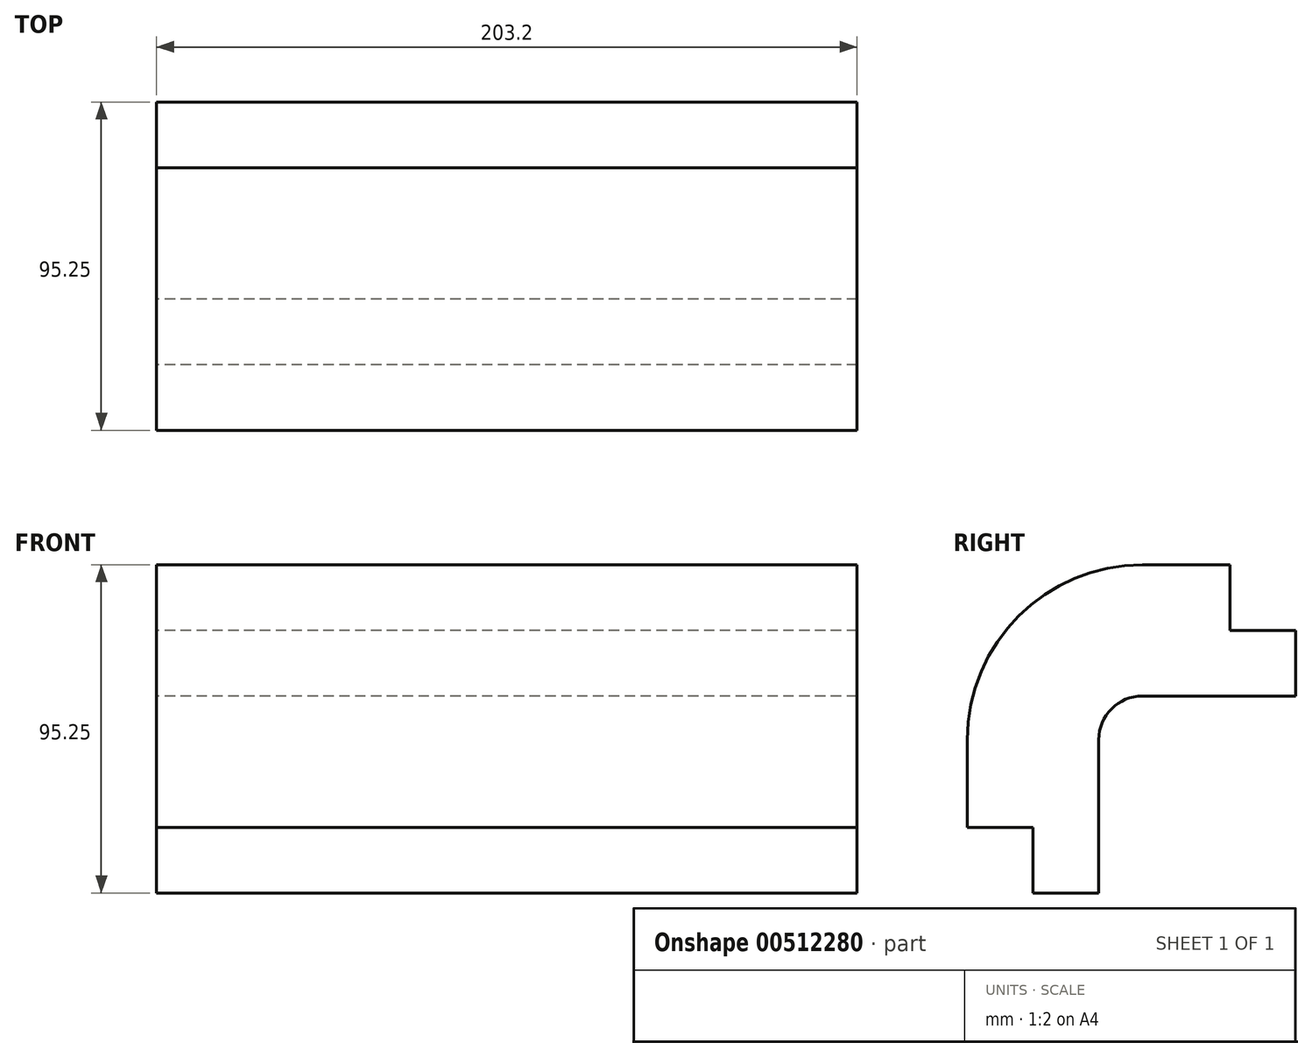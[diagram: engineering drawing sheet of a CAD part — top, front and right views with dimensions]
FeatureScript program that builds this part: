
annotation { "Feature Type Name" : "Feature", "Feature Type Description" : "" }
export const myFeature = defineFeature(function(context is Context, id is Id, definition is map)
    precondition{}
    {
        {
            var Q0;
            Q0=qCreatedBy(makeId("Right.planeOp"),FACE);
            var sketch = newSketch(context, id + "F0", { "sketchPlane" : qUnion([Q0])});
            skLineSegment(sketch, "E0.bottom", {"start": v(0, 0) * mm, "end": v(101.6, 0) * mm});
            skLineSegment(sketch, "E0.top", {"start": v(0, -101.6) * mm, "end": v(101.6, -101.6) * mm});
            skLineSegment(sketch, "E0.left", {"start": v(0, 0) * mm, "end": v(0, -101.6) * mm});
            skLineSegment(sketch, "E0.right", {"start": v(101.6, 0) * mm, "end": v(101.6, -101.6) * mm});
            skArc(sketch, "E1", {"start": v(50.8, 0) * mm, "mid": v(14.88, -14.88) * mm, "end": v(0, -50.8) * mm});
            skLineSegment(sketch, "E2", {"start": v(0, -76.2) * mm, "end": v(19.05, -76.2) * mm});
            skLineSegment(sketch, "E3", {"start": v(19.05, -76.2) * mm, "end": v(19.05, -95.25) * mm});
            skLineSegment(sketch, "E4", {"start": v(19.05, -95.25) * mm, "end": v(38.1, -95.25) * mm});
            skLineSegment(sketch, "E5", {"start": v(38.1, -95.25) * mm, "end": v(38.1, -50.8) * mm});
            skLineSegment(sketch, "E6", {"start": v(76.2, 0) * mm, "end": v(76.2, -19.05) * mm});
            skLineSegment(sketch, "E7", {"start": v(76.2, -19.05) * mm, "end": v(95.25, -19.05) * mm});
            skLineSegment(sketch, "E8", {"start": v(95.25, -19.05) * mm, "end": v(95.25, -38.1) * mm});
            skLineSegment(sketch, "E9", {"start": v(95.25, -38.1) * mm, "end": v(50.8, -38.1) * mm});
            skArc(sketch, "E10", {"start": v(38.1, -50.8) * mm, "mid": v(41.82, -41.82) * mm, "end": v(50.8, -38.1) * mm});
            skSolve(sketch);
        }
        {
            var Q0;
            {var subQ1=sQuery(id+"F0.wireOp",EDGE,"E1");Q0=makeQuery(id+"F0.imprint","IMPRINT",FACE,{"disambiguationData":[TD([[makeQuery(id+"F0.imprint","IMPRINT",EDGE,{"derivedFrom":subQ1}),1.0]])]});}
            extrude(context, id + "F1", {"entities" : qUnion([Q0]), "endBound" : BoundingType.SYMMETRIC, "depth" : 203.2 * mm});
        }
    });
